# Revit family: Banco Bretana
name_source: partatom
category: Furniture
units: mm (PartAtom-declared; Revit-internal decimal feet)

## family parameters
Always vertical = Yes
Cut with Voids When Loaded = No
OmniClass Number = 23.40.20.00
OmniClass Title = General Furniture and Specialties
Room Calculation Point = No
Shared = No
Work Plane-Based = No

## types (2) — shared parameters
A = 1.8 m
Description = Banqueta fabricada con pies de fundición dúctil
Fabricante = BENITO URBAN SL
Ficha Tecnica = https://www.benito.com
H1 = 0.445 m
Material Pies = <By Category>
Material tablones = <By Category>
Type Comments = Anclaje recomendado: Mediante pernos de expansión M10 según superficie y proyecto
URL Producto = https://www.benito.com
zero-valued in all types: Default Elevation

## per-type parameters (varying)
| type | B | Banco Bretana-UM374 | Banco Bretana-UM374B | H | Referencia |
| Banco Bretana-UM374-1800mm | 0.63 m | Yes | No | 0.77 m | UM374 |
| Banco Bretana-UM374B-1800mm | 0.5 m | No | Yes | 0 m | UM374B |

## geometry (parser evidence)
native form markers: Blend x4, Sweep x6
no freeform markers — native parametric forms only
